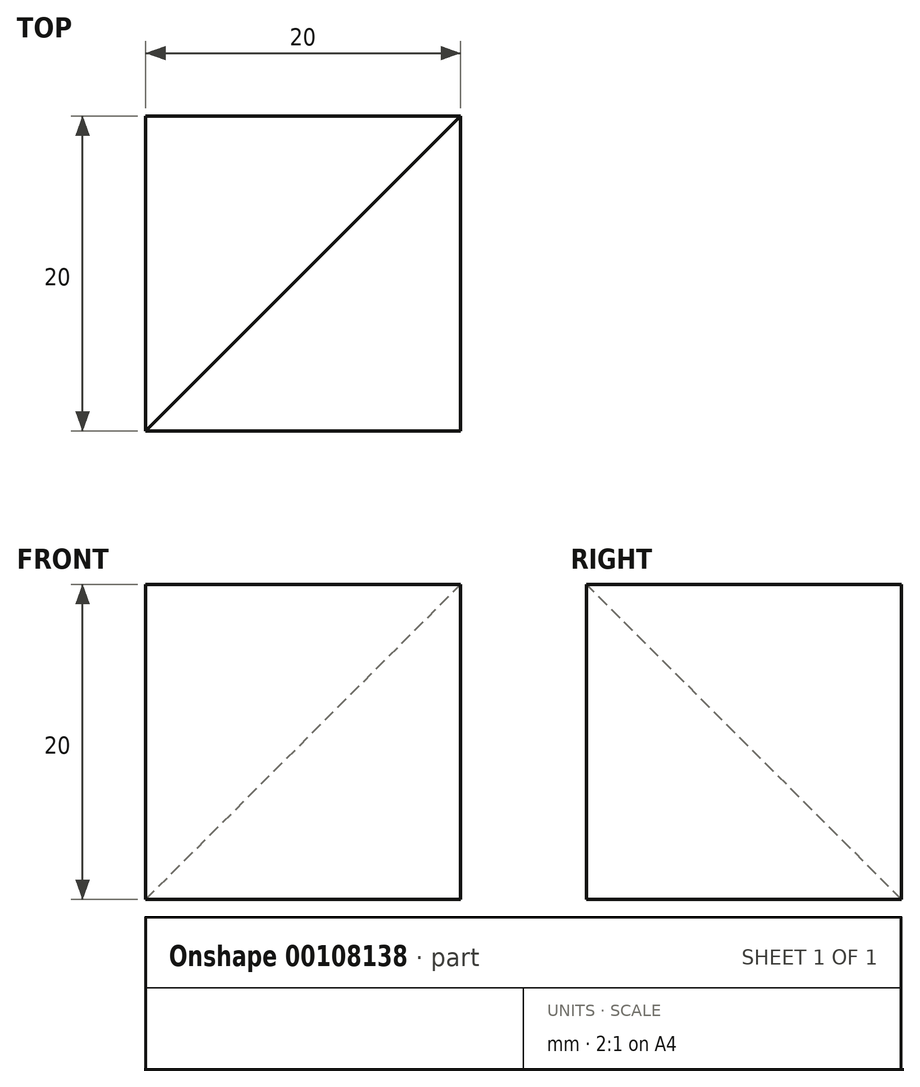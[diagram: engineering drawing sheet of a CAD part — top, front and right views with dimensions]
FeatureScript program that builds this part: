
annotation { "Feature Type Name" : "Feature", "Feature Type Description" : "" }
export const myFeature = defineFeature(function(context is Context, id is Id, definition is map)
    precondition{}
    {
        {
            var Q0;
            Q0=qCreatedBy(makeId("Top.planeOp"),FACE);
            var sketch = newSketch(context, id + "F0", { "sketchPlane" : qUnion([Q0])});
            skLineSegment(sketch, "E0.bottom", {"start": v(10, -10) * mm, "end": v(-10, -10) * mm});
            skLineSegment(sketch, "E0.top", {"start": v(10, 10) * mm, "end": v(-10, 10) * mm});
            skLineSegment(sketch, "E0.left", {"start": v(10, -10) * mm, "end": v(10, 10) * mm});
            skLineSegment(sketch, "E0.right", {"start": v(-10, -10) * mm, "end": v(-10, 10) * mm});
            skPoint(sketch, "E0.middle", {"position": v(0, 0) * mm});
            skSolve(sketch);
        }
        {
            var Q0;
            Q0 = qSketchRegion(id + "F0", true);
            extrude(context, id + "F1", {"entities" : qUnion([Q0]), "depth" : 20 * mm});
        }
        {
            var Q0;
            Q0=makeQuery(id+"F1.opExtrude","CAP_VERTEX",VERTEX,{"disambiguationData":[OSD([sQuery(id+"F0.wireOp",EDGE,"E0.bottom"),sQuery(id+"F0.wireOp",EDGE,"E0.left")])],"isStart":true});
            var Q1;
            Q1=makeQuery(id+"F1.opExtrude","CAP_VERTEX",VERTEX,{"disambiguationData":[OSD([sQuery(id+"F0.wireOp",EDGE,"E0.bottom"),sQuery(id+"F0.wireOp",EDGE,"E0.left")])],"isStart":false});
            var Q2;
            Q2=makeQuery(id+"F1.opExtrude","CAP_VERTEX",VERTEX,{"disambiguationData":[OSD([sQuery(id+"F0.wireOp",EDGE,"E0.top"),sQuery(id+"F0.wireOp",EDGE,"E0.right")])],"isStart":false});
            cPlane(context, id + "F2", {"entities" : qUnion([Q0, Q1, Q2]), "cplaneType" : CPlaneType.THREE_POINT, "offset" : 25 * mm, "width" : 150 * mm, "height" : 150 * mm});
        }
        {
            var Q0;
            Q0=qCreatedBy(id+"F2.planeOp",FACE);
            var sketch = newSketch(context, id + "F3", { "sketchPlane" : qUnion([Q0])});
            skLineSegment(sketch, "E1", {"start": v(14.14, 20) * mm, "end": v(0, 20) * mm});
            skLineSegment(sketch, "E2", {"start": v(0, 20) * mm, "end": v(14.14, 0) * mm});
            skLineSegment(sketch, "E3", {"start": v(14.14, 0) * mm, "end": v(14.14, 20) * mm});
            skSolve(sketch);
        }
        {
            var Q0;
            Q0 = qSketchRegion(id + "F3", true);
            extrude(context, id + "F4", {"entities" : qUnion([Q0]), "operationType" : NewBodyOperationType.REMOVE, "endBound" : BoundingType.SYMMETRIC, "oppositeDirection" : true, "depth" : 30 * mm});
        }
    });
